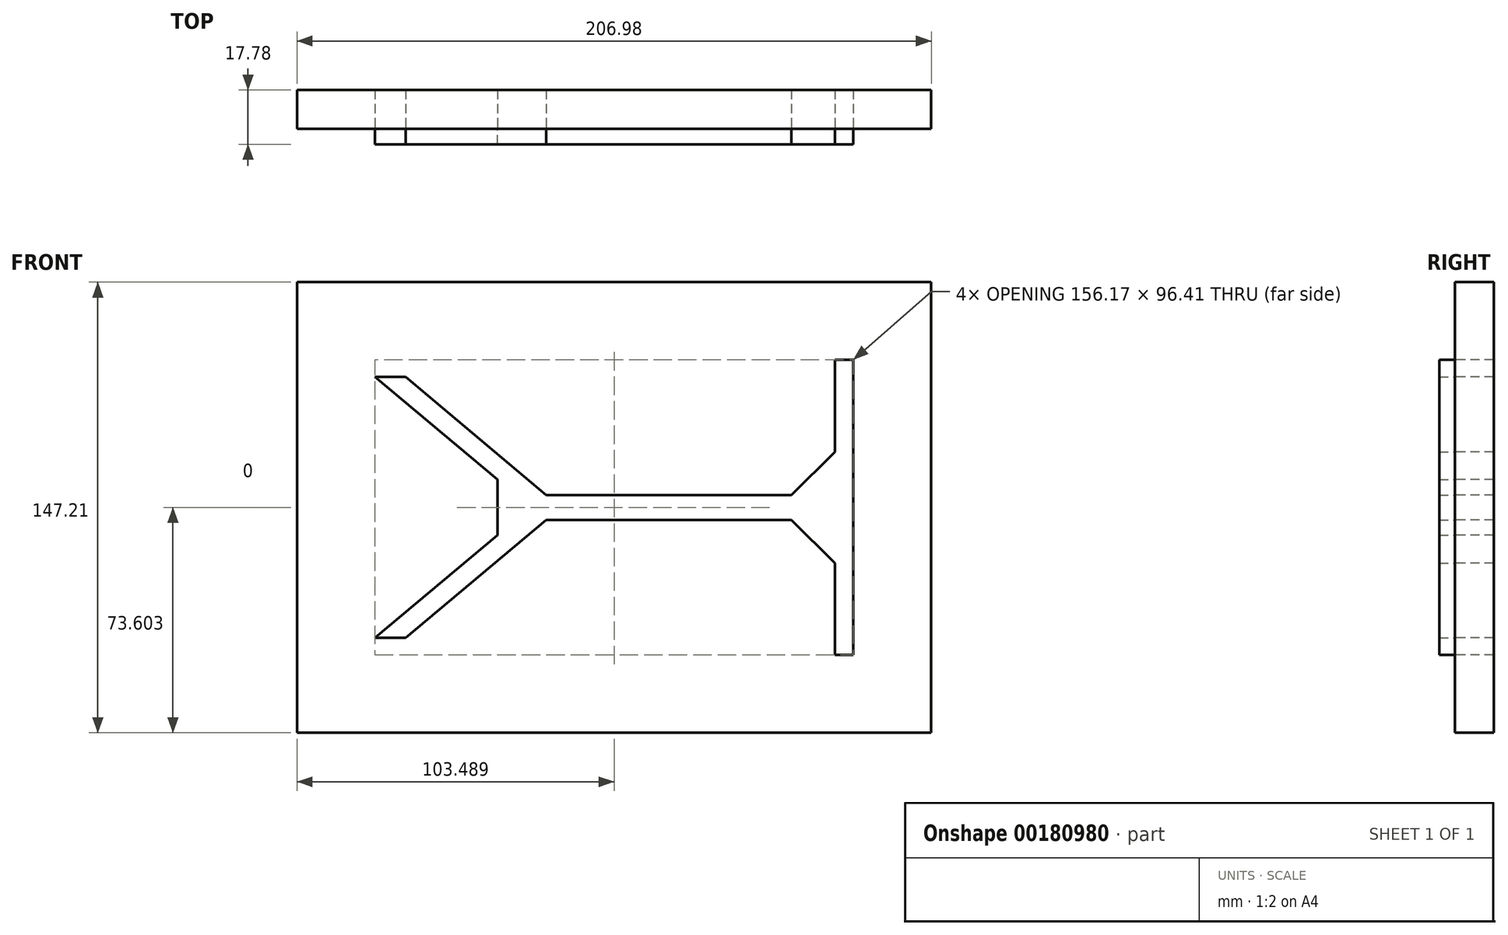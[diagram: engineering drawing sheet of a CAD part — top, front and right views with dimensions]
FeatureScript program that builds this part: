
annotation { "Feature Type Name" : "Feature", "Feature Type Description" : "" }
export const myFeature = defineFeature(function(context is Context, id is Id, definition is map)
    precondition{}
    {
        {
            var Q0;
            Q0=qCreatedBy(makeId("Front.planeOp"),FACE);
            var sketch = newSketch(context, id + "F0", { "sketchPlane" : qUnion([Q0])});
            skLineSegment(sketch, "E0", {"start": v(-1.75, -10.15) * mm, "end": v(78.25, -10.15) * mm});
            skLineSegment(sketch, "E1", {"start": v(-1.75, -10.15) * mm, "end": v(-47.7, 28.42) * mm});
            skLineSegment(sketch, "E2", {"start": v(-47.7, 28.42) * mm, "end": v(-57.7, 28.42) * mm});
            skLineSegment(sketch, "E3", {"start": v(-57.7, 28.42) * mm, "end": v(-17.7, -5.15) * mm});
            skLineSegment(sketch, "E4", {"start": v(-17.7, -5.15) * mm, "end": v(-17.7, -23.27) * mm});
            skLineSegment(sketch, "E5", {"start": v(78.25, -18.27) * mm, "end": v(-1.75, -18.27) * mm});
            skLineSegment(sketch, "E6", {"start": v(-1.75, -18.27) * mm, "end": v(-47.7, -56.84) * mm});
            skLineSegment(sketch, "E7", {"start": v(-47.7, 51.8) * mm, "end": v(-47.7, -103.93) * mm, "construction": true});
            skLineSegment(sketch, "E8", {"start": v(-47.7, -56.84) * mm, "end": v(-57.7, -56.84) * mm});
            skLineSegment(sketch, "E9", {"start": v(-57.7, -56.84) * mm, "end": v(-17.7, -23.27) * mm});
            skLineSegment(sketch, "E10", {"start": v(78.25, -10.15) * mm, "end": v(92.4, 4) * mm});
            skLineSegment(sketch, "E11", {"start": v(92.4, 4) * mm, "end": v(92.4, 34) * mm});
            skLineSegment(sketch, "E12", {"start": v(78.25, -18.27) * mm, "end": v(92.4, -32.41) * mm});
            skLineSegment(sketch, "E13", {"start": v(92.4, -32.41) * mm, "end": v(92.4, -62.41) * mm});
            skLineSegment(sketch, "E14", {"start": v(92.4, 34) * mm, "end": v(98.47, 34) * mm});
            skLineSegment(sketch, "E15", {"start": v(98.47, 34) * mm, "end": v(98.47, -62.41) * mm});
            skLineSegment(sketch, "E16", {"start": v(98.47, -62.41) * mm, "end": v(92.4, -62.41) * mm});
            skSolve(sketch);
        }
        {
            var Q0;
            Q0=makeQuery(id+"F0.imprint","IMPRINT",FACE,{"disambiguationData":[TD([[makeQuery(id+"F0.imprint","IMPRINT",EDGE,{"derivedFrom":sQuery(id+"F0.wireOp",EDGE,"E0")}),-1.0]])]});
            extrude(context, id + "F1", {"entities" : qUnion([Q0]), "depth" : 5.08 * mm});
        }
        {
            var Q0;
            Q0=makeQuery(id+"F1.opExtrude","CAP_FACE",FACE,{"disambiguationData":[OSD([sQuery(id+"F0.wireOp",EDGE,"E0"),sQuery(id+"F0.wireOp",EDGE,"E1"),sQuery(id+"F0.wireOp",EDGE,"E2"),sQuery(id+"F0.wireOp",EDGE,"E3"),sQuery(id+"F0.wireOp",EDGE,"E4"),sQuery(id+"F0.wireOp",EDGE,"E5"),sQuery(id+"F0.wireOp",EDGE,"E6"),sQuery(id+"F0.wireOp",EDGE,"E8"),sQuery(id+"F0.wireOp",EDGE,"E9"),sQuery(id+"F0.wireOp",EDGE,"E10"),sQuery(id+"F0.wireOp",EDGE,"E11"),sQuery(id+"F0.wireOp",EDGE,"E12"),sQuery(id+"F0.wireOp",EDGE,"E13"),sQuery(id+"F0.wireOp",EDGE,"E14"),sQuery(id+"F0.wireOp",EDGE,"E15"),sQuery(id+"F0.wireOp",EDGE,"E16")])],"isStart":true});
            var sketch = newSketch(context, id + "F2", { "sketchPlane" : qUnion([Q0])});
            skLineSegment(sketch, "E17", {"start": v(-123.87, -87.81) * mm, "end": v(83.1, -87.81) * mm});
            skLineSegment(sketch, "E18", {"start": v(-123.87, -87.81) * mm, "end": v(-123.87, 59.4) * mm});
            skLineSegment(sketch, "E19", {"start": v(-123.87, 59.4) * mm, "end": v(83.1, 59.4) * mm});
            skLineSegment(sketch, "E20", {"start": v(83.1, 59.4) * mm, "end": v(83.1, -87.81) * mm});
            skSolve(sketch);
        }
        {
            var Q0;
            Q0=makeQuery(id+"F2.imprint","IMPRINT",FACE,{"disambiguationData":[TD([[makeQuery(id+"F2.imprint","IMPRINT",EDGE,{"derivedFrom":sQuery(id+"F2.wireOp",EDGE,"E17")}),1.0]])]});
            extrude(context, id + "F3", {"entities" : qUnion([Q0]), "depth" : 12.7 * mm});
        }
    });
